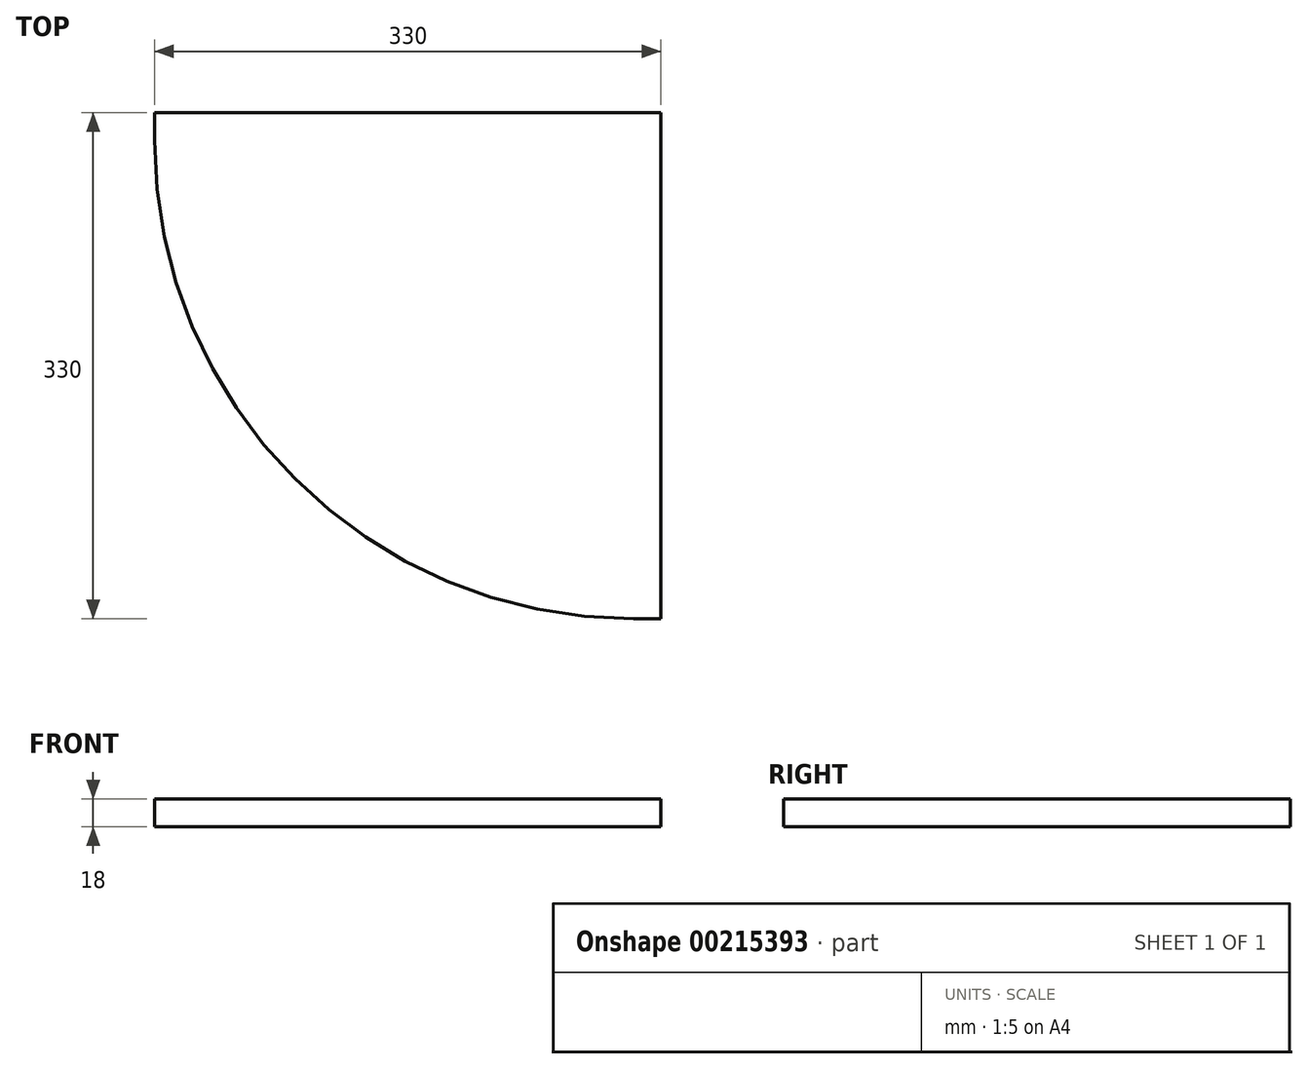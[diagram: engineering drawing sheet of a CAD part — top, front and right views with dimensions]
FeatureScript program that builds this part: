
annotation { "Feature Type Name" : "Feature", "Feature Type Description" : "" }
export const myFeature = defineFeature(function(context is Context, id is Id, definition is map)
    precondition{}
    {
        {
            var Q0;
            Q0=qCreatedBy(makeId("Top.planeOp"),FACE);
            var sketch = newSketch(context, id + "F0", { "sketchPlane" : qUnion([Q0])});
            skLineSegment(sketch, "E0", {"start": v(0, 0) * mm, "end": v(0, 330) * mm});
            skLineSegment(sketch, "E1", {"start": v(0, 330) * mm, "end": v(-330, 330) * mm});
            skLineSegment(sketch, "E2", {"start": v(0, 0) * mm, "end": v(-18, 0) * mm});
            skLineSegment(sketch, "E3", {"start": v(-330, 330) * mm, "end": v(-330, 312) * mm});
            skArc(sketch, "E4", {"start": v(-330, 312) * mm, "mid": v(-238.62, 91.38) * mm, "end": v(-18, 0) * mm});
            skSolve(sketch);
        }
        {
            var Q0;
            Q0=qSketchRegion(id+"F0",true);
            extrude(context, id + "F1", {"entities" : qUnion([Q0]), "depth" : 18 * mm});
        }
    });
